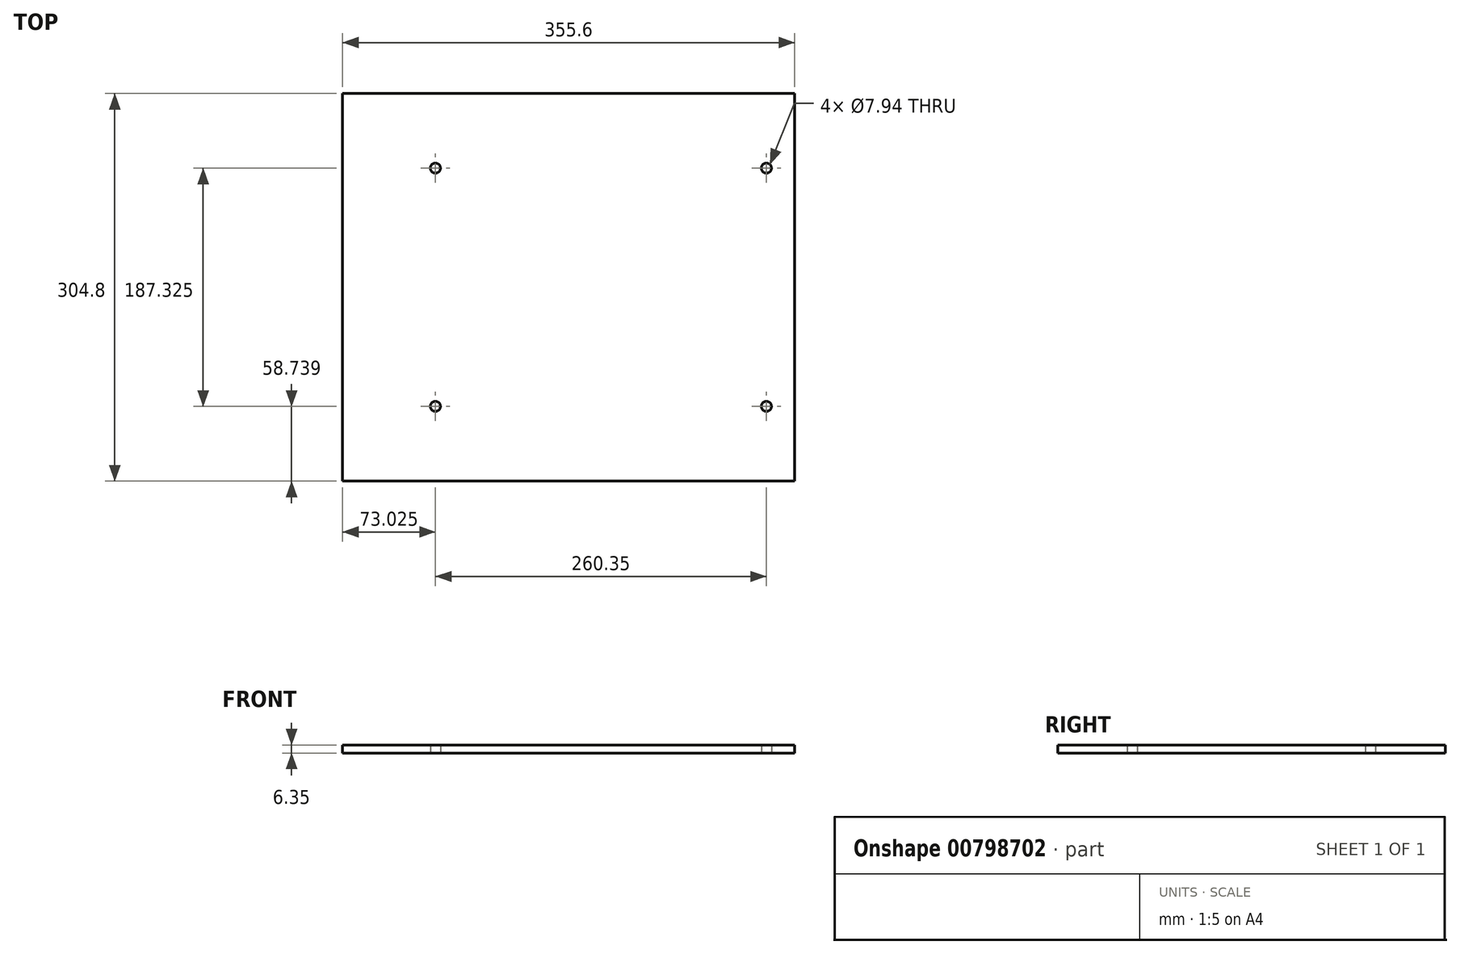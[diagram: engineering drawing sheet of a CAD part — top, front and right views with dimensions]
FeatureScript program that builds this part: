
annotation { "Feature Type Name" : "Feature", "Feature Type Description" : "" }
export const myFeature = defineFeature(function(context is Context, id is Id, definition is map)
    precondition{}
    {
        {
            var Q0;
            Q0=qCreatedBy(makeId("Top.planeOp"),FACE);
            var sketch = newSketch(context, id + "F0", { "sketchPlane" : qUnion([Q0])});
            skLineSegment(sketch, "E0.bottom", {"start": v(0, 4.6) * mm, "end": v(355.6, 4.6) * mm});
            skLineSegment(sketch, "E0.top", {"start": v(0, 309.4) * mm, "end": v(355.6, 309.4) * mm});
            skLineSegment(sketch, "E0.left", {"start": v(0, 4.6) * mm, "end": v(0, 309.4) * mm});
            skLineSegment(sketch, "E0.right", {"start": v(355.6, 4.6) * mm, "end": v(355.6, 309.4) * mm});
            skCircle(sketch, "E1", {"center": v(333.38, 63.33) * mm, "radius": 3.97 * mm});
            skCircle(sketch, "E2.0.1.0", {"center": v(333.38, 250.65) * mm, "radius": 3.97 * mm});
            skCircle(sketch, "E2.1.0.0", {"center": v(73.03, 63.33) * mm, "radius": 3.97 * mm});
            skCircle(sketch, "E2.1.1.0", {"center": v(73.03, 250.65) * mm, "radius": 3.97 * mm});
            skLineSegment(sketch, "E2.direction1", {"start": v(333.38, 63.33) * mm, "end": v(73.03, 63.33) * mm, "construction": true});
            skLineSegment(sketch, "E2.direction2", {"start": v(333.38, 63.33) * mm, "end": v(333.38, 250.65) * mm, "construction": true});
            skSolve(sketch);
        }
        {
            var Q0;
            Q0=qSketchRegion(id+"F0",true);
            extrude(context, id + "F1", {"entities" : qUnion([Q0]), "depth" : 6.35 * mm, "offsetDistance" : 25.4 * mm});
        }
    });
